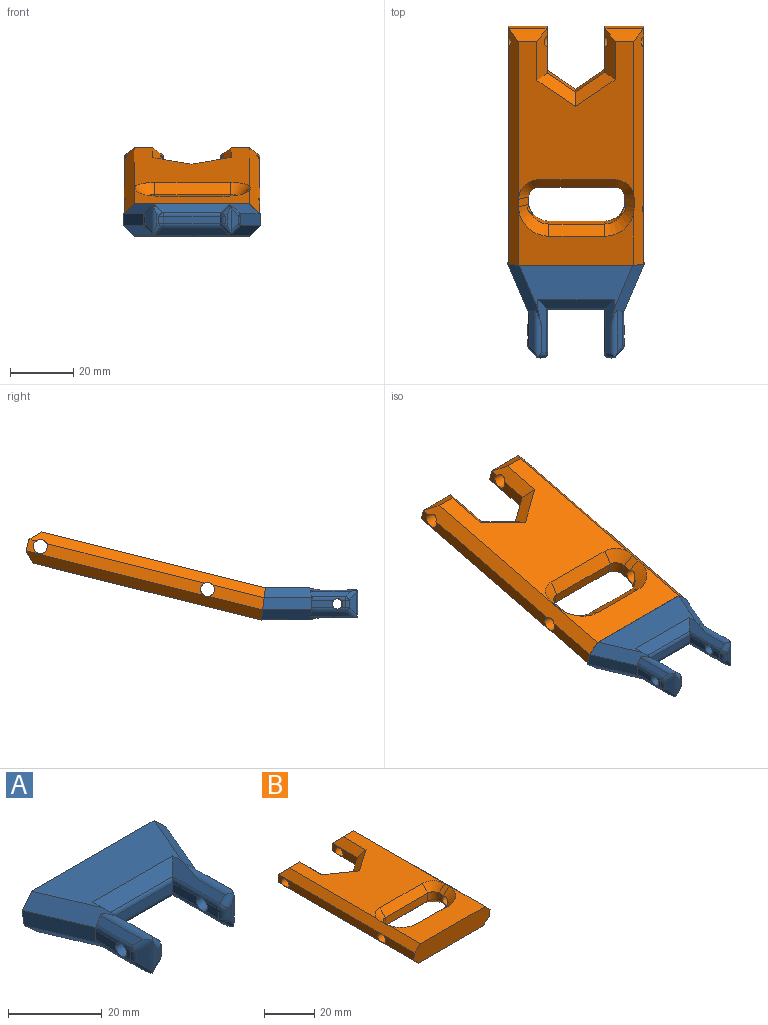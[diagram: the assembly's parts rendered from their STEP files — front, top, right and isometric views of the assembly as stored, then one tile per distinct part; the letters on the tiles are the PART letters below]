
ASSEMBLY  parts=2 mates=1
PART A: 70 faces, bbox 43.4x30.5x10.2 mm
  f0: plane 7.06x2.46mm, normal (1,0.01,0), area 16.3mm2, adj f8,f17,f34,f38
  f1: plane 6.78x2.44mm, normal (-1,0.01,0), area 15.6mm2, adj f10,f16,f51,f58
  f2: plane 7.48x2.45mm, normal (1,0,0), area 17.3mm2, adj f4,f16,f52,f63
  f3: plane 7.63x2.45mm, normal (-1,0,0), area 17.7mm2, adj f4,f17,f46,f53
  f4: plane 17.78x2.44mm, normal (0,-1,0), area 43.4mm2, adj f2,f3,f49,f57
  f5: plane 3.75x2.45mm, normal (-1,0,0), area 8.2mm2, adj f17,f46,f47,f53
  f6: plane 4.06x0.81mm, normal (0,-1,0), area 2.6mm2, adj f39,f43,f47,f48
  f7: plane 2.46x1.47mm, normal (1,0.01,0), area 2.6mm2, adj f17,f34,f37,f38
  f8: plane 15.8x6.73mm, normal (0.92,-0.39,0), area 63.2mm2, adj f0,f9,f18,f19,f34,f38
  f9: plane 43.4x10.16mm, normal (0,0.99,-0.12), area 420.2mm2, adj f8,f10,f14,f15,f18,f19,f25,f26
  f10: plane 15.8x6.73mm, normal (-0.92,-0.39,0), area 63.2mm2, adj f1,f9,f25,f26,f51,f58
  f11: plane 2.44x1.71mm, normal (-1,0.01,0), area 3.3mm2, adj f16,f51,f58,f59
  f12: plane 4.06x0.81mm, normal (0,-1,0), area 2.6mm2, adj f61,f62,f65,f68
  f13: plane 3.91x2.45mm, normal (1,0,0), area 8.6mm2, adj f16,f52,f62,f63
  f14: plane 36.83x14.91mm, normal (0,0,1), area 385.3mm2, adj f9,f18,f24,f25,f30,f31
  f15: plane 35.77x13.66mm, normal (0,0,-1), area 340mm2, adj f9,f19,f23,f26,f32,f33
  f16: cylinder r=1.65mm len=6.33mm, axis (-1,0.01,0), area 64.9mm2, adj f1,f2,f11,f13,f51,f52,f58,f63
  f17: cylinder r=1.65mm len=6.35mm, axis (-1,0.01,0), area 65mm2, adj f0,f3,f5,f7,f34,f38,f46,f53
  f18: plane 20.83x10.85mm, normal (0.65,-0.28,0.71), area 77mm2, adj f8,f9,f14,f20,f31,f34,f35
  f19: plane 19.97x10.65mm, normal (0.65,-0.28,-0.71), area 72.8mm2, adj f8,f9,f15,f21,f32,f38,f45
  f20: plane 12.62x1.56mm, normal (0.71,0.01,0.71), area 24.6mm2, adj f18,f34,f35,f40
  f21: plane 12.62x1.56mm, normal (0.71,0.01,-0.71), area 24.6mm2, adj f19,f38,f44,f45
  f22: plane 6.89x2.23mm, normal (0.71,-0.7,0), area 14.6mm2, adj f37,f40,f43,f44
  f23: plane 24.13x2.69mm, normal (0,-0.71,-0.71), area 81.6mm2, adj f15,f32,f33,f57
  f24: plane 24.13x2.69mm, normal (0,-0.71,0.71), area 81.6mm2, adj f14,f30,f31,f49
  f25: plane 20.83x10.85mm, normal (-0.65,-0.28,0.71), area 77mm2, adj f9,f10,f14,f27,f30,f51,f55
  f26: plane 19.97x10.65mm, normal (-0.65,-0.28,-0.71), area 72.8mm2, adj f9,f10,f15,f28,f33,f58,f69
  f27: plane 12.62x1.56mm, normal (-0.71,0.01,0.71), area 24.6mm2, adj f25,f51,f55,f60
  f28: plane 12.62x1.56mm, normal (-0.71,0.01,-0.71), area 24.6mm2, adj f26,f58,f67,f69
  f29: plane 6.89x2.23mm, normal (-0.71,-0.7,0), area 14.6mm2, adj f59,f60,f65,f67
  f30: plane 16.76x2.69mm, normal (0.71,0,0.71), area 40.2mm2, adj f14,f24,f25,f52,f55,f61
  f31: plane 16.76x2.69mm, normal (-0.71,0,0.71), area 40.2mm2, adj f14,f18,f24,f35,f39,f46
  f32: plane 16.76x2.69mm, normal (-0.71,0,-0.71), area 40.2mm2, adj f15,f19,f23,f45,f48,f53
  f33: plane 16.76x2.69mm, normal (0.71,0,-0.71), area 40.2mm2, adj f15,f23,f26,f63,f68,f69
  f34: cylinder r=1.65mm len=10.82mm, axis (-0.01,1,0), area 13.1mm2, adj f0,f7,f8,f17,f18,f20,f36
  f35: cylinder r=1.65mm len=14.64mm, axis (0,-1,0), area 31.1mm2, adj f18,f20,f31,f39,f40
  f36: sphere r=1.65mm, area 0.9mm2, adj f34,f37,f40
  f37: cylinder r=1.65mm len=2.44mm, axis (0,0,-1), area 3.2mm2, adj f7,f22,f36,f41
  f38: cylinder r=1.65mm len=10.82mm, axis (-0.01,1,0), area 13.1mm2, adj f0,f7,f8,f17,f19,f21,f41
  f39: cylinder r=1.65mm len=3.6mm, axis (0.71,0,0.71), area 6.9mm2, adj f6,f31,f35,f40,f42,f43
  f40: cylinder r=1.65mm len=3.85mm, axis (0.57,0.58,-0.58), area 6.8mm2, adj f20,f22,f35,f36,f39,f43
  f41: sphere r=1.65mm, area 0.9mm2, adj f37,f38,f44
  f42: sphere r=1.65mm, area 2.1mm2, adj f39,f46,f47
  f43: cylinder r=1.65mm len=8.32mm, axis (0,0,1), area 8.7mm2, adj f6,f22,f39,f40,f44,f48
  f44: cylinder r=1.65mm len=3.85mm, axis (0.57,0.58,0.58), area 6.8mm2, adj f21,f22,f41,f43,f45,f48
  f45: cylinder r=1.65mm len=14.64mm, axis (0,1,0), area 31.1mm2, adj f19,f21,f32,f44,f48
  f46: cylinder r=1.65mm len=14.07mm, axis (0,-1,0), area 17.2mm2, adj f3,f5,f17,f31,f42,f49
  f47: cylinder r=1.65mm len=2.44mm, axis (0,0,-1), area 6.3mm2, adj f5,f6,f42,f50
  f48: cylinder r=1.65mm len=3.6mm, axis (0.71,0,-0.71), area 6.9mm2, adj f6,f32,f43,f44,f45,f50
  f49: cylinder r=1.65mm len=18.75mm, axis (1,0,0), area 23.5mm2, adj f4,f24,f46,f52
  f50: sphere r=1.65mm, area 2.1mm2, adj f47,f48,f53
  f51: cylinder r=1.65mm len=10.82mm, axis (-0.01,-1,0), area 13.1mm2, adj f1,f10,f11,f16,f25,f27,f54
  f52: cylinder r=1.65mm len=14.07mm, axis (0,1,0), area 17.2mm2, adj f2,f13,f16,f30,f49,f56
  f53: cylinder r=1.65mm len=14.07mm, axis (0,-1,0), area 17.2mm2, adj f3,f5,f17,f32,f50,f57
  f54: sphere r=1.65mm, area 0.9mm2, adj f51,f59,f60
  f55: cylinder r=1.65mm len=14.64mm, axis (0,-1,0), area 31.1mm2, adj f25,f27,f30,f60,f61
  f56: sphere r=1.65mm, area 2.1mm2, adj f52,f61,f62
  f57: cylinder r=1.65mm len=18.75mm, axis (1,0,0), area 23.5mm2, adj f4,f23,f53,f63
  f58: cylinder r=1.65mm len=10.82mm, axis (-0.01,-1,0), area 13.1mm2, adj f1,f10,f11,f16,f26,f28,f64
  f59: cylinder r=1.65mm len=2.44mm, axis (0,0,-1), area 3.2mm2, adj f11,f29,f54,f64
  f60: cylinder r=1.65mm len=3.85mm, axis (-0.57,0.58,-0.58), area 6.8mm2, adj f27,f29,f54,f55,f61,f65
  f61: cylinder r=1.65mm len=3.6mm, axis (-0.71,0,0.71), area 6.9mm2, adj f12,f30,f55,f56,f60,f65
  f62: cylinder r=1.65mm len=2.44mm, axis (0,0,1), area 6.3mm2, adj f12,f13,f56,f66
  f63: cylinder r=1.65mm len=14.07mm, axis (0,1,0), area 17.2mm2, adj f2,f13,f16,f33,f57,f66
  f64: sphere r=1.65mm, area 0.9mm2, adj f58,f59,f67
  f65: cylinder r=1.65mm len=8.32mm, axis (0,0,1), area 8.7mm2, adj f12,f29,f60,f61,f67,f68
  f66: sphere r=1.65mm, area 2.1mm2, adj f62,f63,f68
  f67: cylinder r=1.65mm len=3.85mm, axis (-0.57,0.58,0.58), area 6.8mm2, adj f28,f29,f64,f65,f68,f69
  f68: cylinder r=1.65mm len=3.6mm, axis (-0.71,0,-0.71), area 6.9mm2, adj f12,f33,f65,f66,f67,f69
  f69: cylinder r=1.65mm len=14.64mm, axis (0,1,0), area 31.1mm2, adj f26,f28,f33,f67,f68
PART B: 61 faces, bbox 42.7x77.3x10.2 mm
  f0: plane 57.79x3.81mm, normal (1,0,0), area 202.7mm2, adj f22,f26,f27,f29,f45
  f1: plane 57.79x3.81mm, normal (-1,0,0), area 202.7mm2, adj f12,f25,f28,f39,f55
  f2: cylinder r=6.35mm len=5.97mm, axis (0,0,-1), area 24.7mm2, adj f16,f27,f38,f59
  f3: cylinder r=6.35mm len=0.09mm, axis (0,0,-1), area 0mm2, adj f21,f27,f38
  f4: cylinder r=6.35mm len=0.72mm, axis (0,0,-1), area 0.1mm2, adj f17,f28,f58
  f5: cylinder r=6.35mm len=5.97mm, axis (0,0,-1), area 24.7mm2, adj f16,f28,f37,f58
  f6: cylinder r=6.35mm len=0.09mm, axis (0,0,-1), area 0mm2, adj f17,f28,f37
  f7: cylinder r=6.35mm len=0.72mm, axis (0,0,-1), area 0.1mm2, adj f21,f27,f59
  f8: plane 14.36x3.81mm, normal (-1,0,0), area 41.6mm2, adj f9,f22,f26,f31,f47
  f9: plane 8.94x6.21mm, normal (-0.57,0.82,0), area 41.5mm2, adj f8,f10,f32,f48
  f10: plane 9.34x6.49mm, normal (0.57,0.82,0), area 43.3mm2, adj f9,f11,f33,f49
  f11: plane 14.08x3.81mm, normal (1,0,0), area 40.5mm2, adj f10,f12,f25,f34,f50
  f12: plane 12.19x3.81mm, normal (0,1,0), area 46.5mm2, adj f1,f11,f36,f52
  f13: plane 17.71x3.81mm, normal (-1,0,0), area 62.2mm2, adj f14,f28,f39,f55
  f14: plane 42.67x10.16mm, normal (0,-0.99,-0.12), area 416.5mm2, adj f13,f15,f23,f24,f29,f39,f45,f55
  f15: plane 17.71x3.81mm, normal (1,0,0), area 62.2mm2, adj f14,f27,f29,f45
  f16: plane 17.55x3.81mm, normal (0,1,0), area 66.9mm2, adj f2,f5,f35,f60
  f17: plane 3.81x2.47mm, normal (1,0,0), area 7.7mm2, adj f4,f6,f18,f28,f40,f56
  f18: cylinder r=3.17mm len=3.81mm, axis (0,0,-1), area 19mm2, adj f17,f19,f42,f53
  f19: plane 23.9x3.81mm, normal (0,-1,0), area 91.1mm2, adj f18,f20,f44,f51
  f20: cylinder r=3.17mm len=3.81mm, axis (0,0,-1), area 19mm2, adj f19,f21,f43,f54
  f21: plane 3.81x2.47mm, normal (-1,0,0), area 7.7mm2, adj f3,f7,f20,f27,f41,f57
  f22: plane 12.19x3.81mm, normal (0,1,0), area 46.5mm2, adj f0,f8,f30,f46
  f23: plane 74.17x36.32mm, normal (0,0,1), area 1662.5mm2, adj f14,f45,f46,f47,f48,f49,f50,f51
  f24: plane 72.92x36.32mm, normal (0,0,-1), area 1617.2mm2, adj f14,f29,f30,f31,f32,f33,f34,f35
  f25: cylinder r=2.2mm len=12.19mm, axis (1,0,0), area 164.1mm2, adj f1,f11,f34,f39
  f26: cylinder r=2.2mm len=12.19mm, axis (1,0,0), area 164.1mm2, adj f0,f8,f29,f31
  f27: cylinder r=2.2mm len=7.57mm, axis (1,0,0), area 91.8mm2, adj f0,f2,f3,f7,f15,f21,f29,f38
  f28: cylinder r=2.2mm len=7.15mm, axis (1,0,0), area 86.1mm2, adj f1,f4,f5,f6,f13,f17,f37,f39
  f29: plane 76.49x3.18mm, normal (0.71,0,-0.71), area 331.3mm2, adj f0,f14,f15,f24,f26,f27,f30
  f30: plane 12.19x3.18mm, normal (0,0.71,-0.71), area 40.5mm2, adj f22,f24,f29,f31
  f31: plane 16.02x3.18mm, normal (-0.71,0,-0.71), area 58.1mm2, adj f8,f24,f26,f30,f32
  f32: plane 12.12x10.08mm, normal (-0.4,0.58,-0.71), area 57.6mm2, adj f9,f24,f31,f33
  f33: plane 12.52x10.35mm, normal (0.4,0.58,-0.71), area 59.8mm2, adj f10,f24,f32,f34
  f34: plane 15.74x3.18mm, normal (0.71,0,-0.71), area 56.9mm2, adj f11,f24,f25,f33,f36
  f35: plane 17.55x3.18mm, normal (0,0.71,-0.71), area 78.8mm2, adj f16,f24,f37,f38
  f36: plane 12.19x3.18mm, normal (0,0.71,-0.71), area 40.5mm2, adj f12,f24,f34,f39
  f37: cone r=9.53mm half-angle=45deg, axis (0,0,-1), area 54.3mm2, adj f5,f6,f24,f28,f35,f39,f40
  f38: cone r=9.53mm half-angle=45deg, axis (0,0,-1), area 54.7mm2, adj f2,f3,f24,f27,f35,f41
  f39: plane 76.49x3.18mm, normal (-0.71,0,-0.71), area 329.9mm2, adj f1,f13,f14,f24,f25,f28,f36,f37
  f40: plane 3x3mm, normal (0.71,0,-0.71), area 10.5mm2, adj f17,f37,f39,f42
  f41: plane 3.18x3.18mm, normal (-0.71,0,-0.71), area 11.1mm2, adj f21,f24,f38,f43
  f42: cone r=6.35mm half-angle=45deg, axis (0,0,-1), area 33.2mm2, adj f18,f24,f39,f40,f44
  f43: cone r=6.35mm half-angle=45deg, axis (0,0,-1), area 33.6mm2, adj f20,f24,f41,f44
  f44: plane 23.9x3.18mm, normal (0,-0.71,-0.71), area 107.3mm2, adj f19,f24,f42,f43
  f45: plane 77.34x3.18mm, normal (0.71,0,0.71), area 339.1mm2, adj f0,f14,f15,f23,f27,f46
  f46: plane 12.19x3.18mm, normal (0,0.71,0.71), area 40.5mm2, adj f22,f23,f45,f47
  f47: plane 16.02x3.18mm, normal (-0.71,0,0.71), area 61.1mm2, adj f8,f23,f46,f48
  f48: plane 12.12x10.08mm, normal (-0.4,0.58,0.71), area 57.6mm2, adj f9,f23,f47,f49
  f49: plane 12.52x10.35mm, normal (0.4,0.58,0.71), area 59.8mm2, adj f10,f23,f48,f50
  f50: plane 15.74x3.18mm, normal (0.71,0,0.71), area 59.8mm2, adj f11,f23,f49,f52
  f51: plane 23.9x3.18mm, normal (0,-0.71,0.71), area 107.3mm2, adj f19,f23,f53,f54
  f52: plane 12.19x3.18mm, normal (0,0.71,0.71), area 40.5mm2, adj f12,f23,f50,f55
  f53: cone r=3.17mm half-angle=45deg, axis (0,0,1), area 33.2mm2, adj f18,f23,f51,f55,f56
  f54: cone r=3.17mm half-angle=45deg, axis (0,0,1), area 33.6mm2, adj f20,f23,f51,f57
  f55: plane 77.34x3.18mm, normal (-0.71,0,0.71), area 337.8mm2, adj f1,f13,f14,f23,f28,f52,f53,f56
  f56: plane 3x3mm, normal (0.71,0,0.71), area 10.5mm2, adj f17,f53,f55,f58
  f57: plane 3.18x3.18mm, normal (-0.71,0,0.71), area 11.1mm2, adj f21,f23,f54,f59
  f58: cone r=6.35mm half-angle=45deg, axis (0,0,1), area 55.4mm2, adj f4,f5,f23,f28,f55,f56,f60
  f59: cone r=6.35mm half-angle=45deg, axis (0,0,1), area 55.8mm2, adj f2,f7,f23,f27,f57,f60
  f60: plane 17.55x3.18mm, normal (0,0.71,0.71), area 78.8mm2, adj f16,f23,f58,f59
PLACE A rot(axis=(0,-1,0),180deg) t=(-6.49,-56.52,-1.01)mm
PLACE B rot(axis=(0,-0.99,-0.12),180deg) t=(-5.9,7.96,9.73)mm
MATE fastened B.f14 <-> A.f9  axis (0,-0.99,-0.12) through (-2.54,-34.56,-6.11)mm
